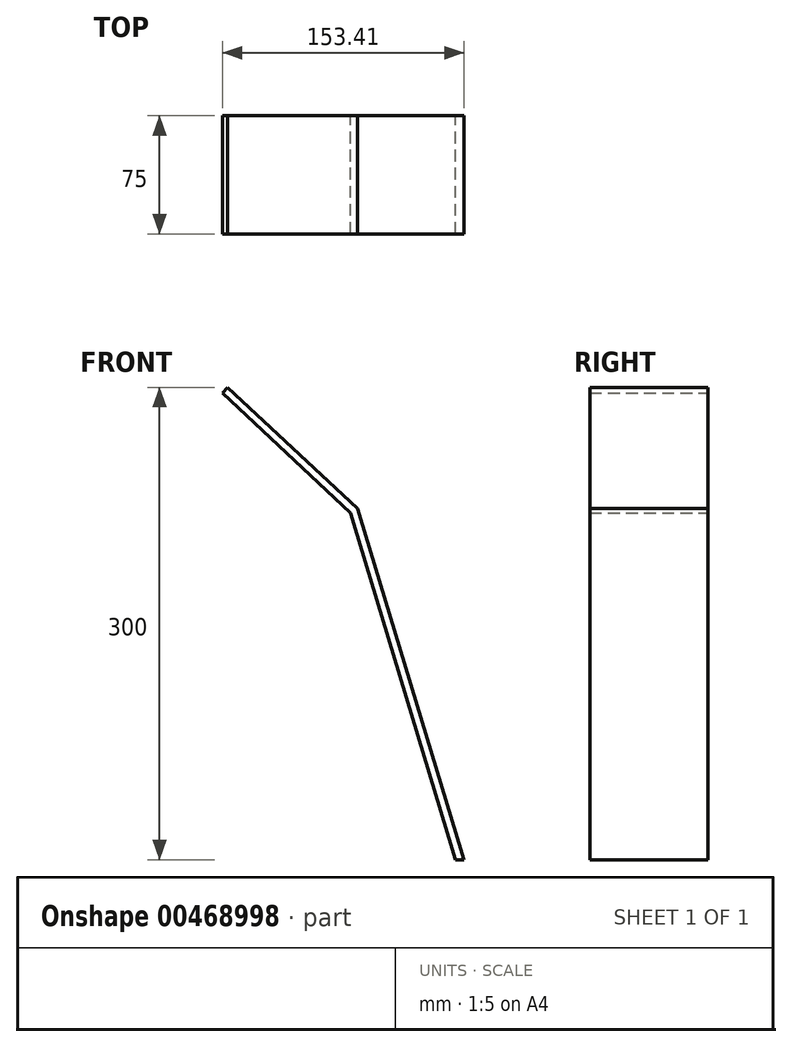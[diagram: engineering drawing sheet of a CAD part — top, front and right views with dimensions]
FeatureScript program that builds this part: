
annotation { "Feature Type Name" : "Feature", "Feature Type Description" : "" }
export const myFeature = defineFeature(function(context is Context, id is Id, definition is map)
    precondition{}
    {
        {
            var Q0;
            Q0=qCreatedBy(makeId("Front.planeOp"),FACE);
            var sketch = newSketch(context, id + "F0", { "sketchPlane" : qUnion([Q0])});
            skLineSegment(sketch, "E0.bottom", {"start": v(0, 0) * mm, "end": v(-5.22, 0) * mm});
            skLineSegment(sketch, "E1", {"start": v(0, 0) * mm, "end": v(-67.5, 222.98) * mm});
            skLineSegment(sketch, "E2", {"start": v(-67.5, 222.98) * mm, "end": v(-150, 300) * mm});
            skLineSegment(sketch, "E3.0", {"start": v(-71.9, 220.24) * mm, "end": v(-153.41, 296.35) * mm});
            skLineSegment(sketch, "E3.1", {"start": v(-8.7, 11.49) * mm, "end": v(-71.9, 220.24) * mm});
            skLineSegment(sketch, "E4", {"start": v(-153.41, 296.35) * mm, "end": v(-150, 300) * mm});
            skLineSegment(sketch, "E5", {"start": v(-8.7, 11.49) * mm, "end": v(-5.22, 0) * mm});
            skSolve(sketch);
        }
        {
            var Q0;
            Q0=makeQuery(id+"F0.imprint","IMPRINT",FACE,{"disambiguationData":[TD([[makeQuery(id+"F0.imprint","IMPRINT",EDGE,{"derivedFrom":sQuery(id+"F0.wireOp",EDGE,"E0.bottom")}),-1.0]])]});
            extrude(context, id + "F1", {"entities" : qUnion([Q0]), "depth" : 75 * mm});
        }
    });
